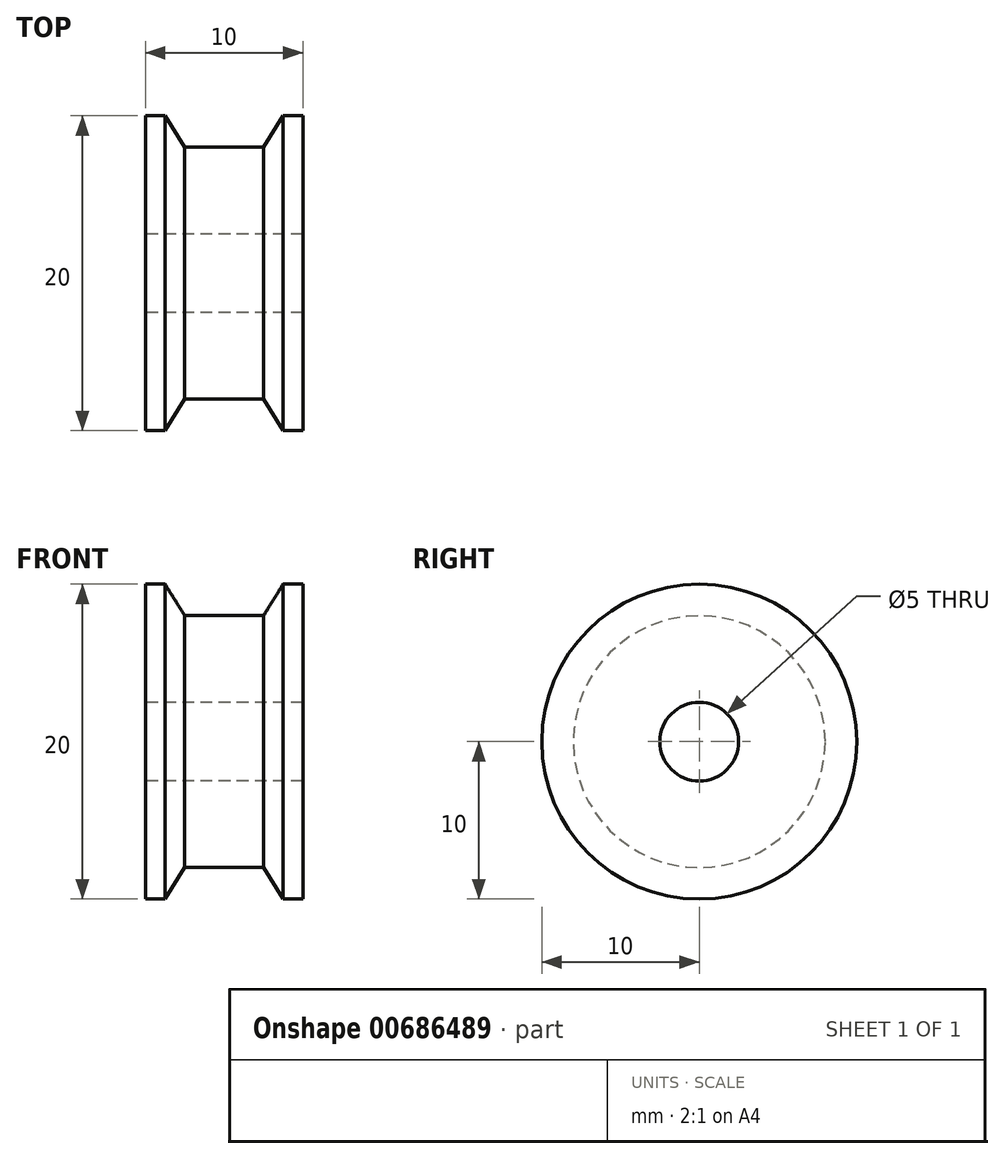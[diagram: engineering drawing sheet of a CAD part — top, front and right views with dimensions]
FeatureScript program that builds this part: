
annotation { "Feature Type Name" : "Feature", "Feature Type Description" : "" }
export const myFeature = defineFeature(function(context is Context, id is Id, definition is map)
    precondition{}
    {
        {
            var Q0;
            Q0=qCreatedBy(makeId("Front.planeOp"),FACE);
            var sketch = newSketch(context, id + "F0", { "sketchPlane" : qUnion([Q0])});
            skLineSegment(sketch, "E0.bottom", {"start": v(-5, 0) * mm, "end": v(5, 0) * mm});
            skLineSegment(sketch, "E0.left", {"start": v(-5, 0) * mm, "end": v(-5, 7.5) * mm});
            skLineSegment(sketch, "E0.right", {"start": v(5, 0) * mm, "end": v(5, 7.5) * mm});
            skLineSegment(sketch, "E1", {"start": v(-2.5, 5.5) * mm, "end": v(2.5, 5.5) * mm});
            skLineSegment(sketch, "E2", {"start": v(-15.17, -2.5) * mm, "end": v(24.62, -2.5) * mm});
            skLineSegment(sketch, "E3", {"start": v(-5, 7.5) * mm, "end": v(-3.75, 7.5) * mm});
            skLineSegment(sketch, "E4", {"start": v(-3.75, 7.5) * mm, "end": v(-2.5, 5.5) * mm});
            skLineSegment(sketch, "E5", {"start": v(2.5, 5.5) * mm, "end": v(3.75, 7.5) * mm});
            skLineSegment(sketch, "E6", {"start": v(3.75, 7.5) * mm, "end": v(5, 7.5) * mm});
            skSolve(sketch);
        }
        {
            var Q0;
            Q0 = qSketchRegion(id + "F0", true);
            var Q1;
            Q1=sQuery(id+"F0.wireOp",EDGE,"E2");
            revolve(context, id + "F1", {"entities" : qUnion([Q0]), "axis" : qUnion([Q1]), "revolveType" : RevolveType.FULL});
        }
    });
